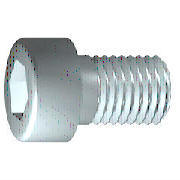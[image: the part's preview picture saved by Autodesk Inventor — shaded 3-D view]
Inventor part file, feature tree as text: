
AUTODESK INVENTOR PART (.ipt)
format: ipt  version: 2020 (Build 240168000, 168)  size: 187,904 bytes
history: native  units: mm (DEFAULTED — no unit token found)
features: sketch x2, extrude x1, plane x1, fillet x1
ambient origin geometry x7: Origin, YZ Plane, XY Plane, X Axis, Y Axis, Z Axis, Center Point
bodies: Solid1 (feature_tree), Body (feature_tree)
feature tree (5):
  extrude  "Slot"  Depth=3.0mm
  plane  "Work Plane1"
  fillet  "Fillet2"  Radius=3.0mm
  sketch  "Sketch1"  dims[d1=18.0mm d2=0.306825mm d3=3.0mm]
  sketch  "Sketch2"  dims[d4=1.3mm d5=60.0deg d6=3.0mm d7=3.0mm d8=2.886751mm d9=5.5mm d10=90.0deg d11=10.0mm d12=0.0mm d13=18.0mm d14=0.0mm d15=0.306725mm d16=0.306725mm d17=0.3mm d19=0.0mm d26=30.0mm d27=45.0deg d28=0.0mm d29=0.0mm d30=0.1mm]
